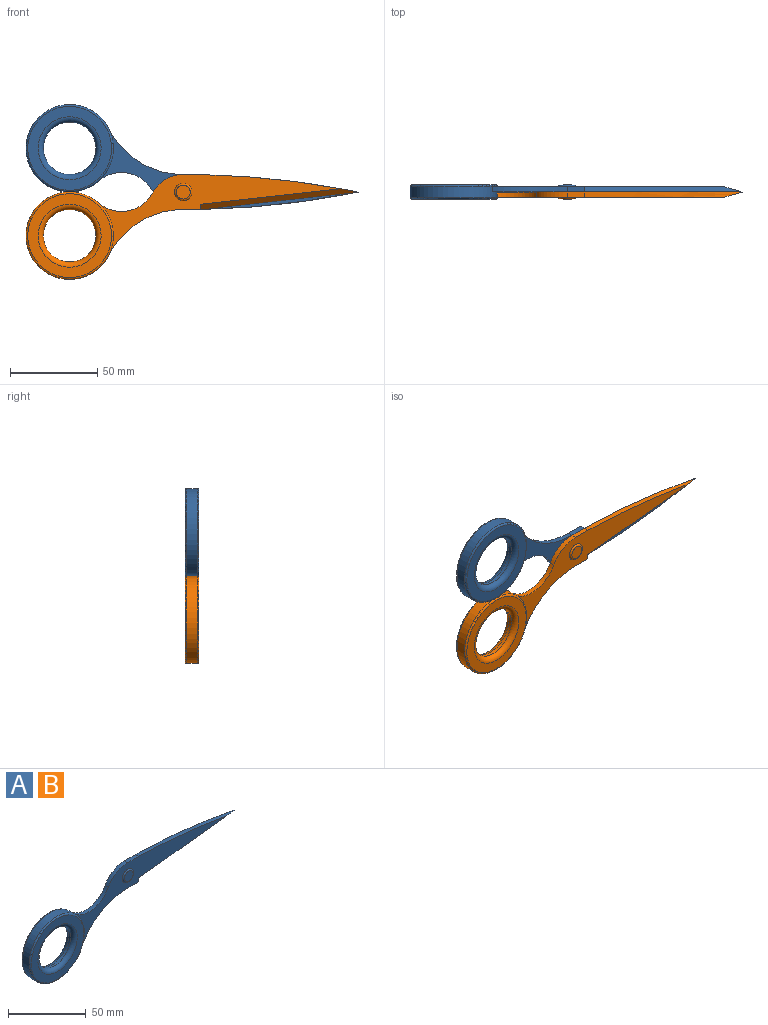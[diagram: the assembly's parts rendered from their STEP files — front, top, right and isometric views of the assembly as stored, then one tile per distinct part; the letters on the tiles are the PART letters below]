
ASSEMBLY  parts=2 mates=1
PART A: 20 faces, bbox 192.1x8x62.1 mm
  f0: plane 138.66x46.27mm, normal (0,-1,0), area 1503.1mm2, adj f2,f3,f4,f5,f6,f8,f13,f14
  f1: plane 148.5x46.27mm, normal (0,1,0), area 1837mm2, adj f2,f3,f4,f5,f6,f7,f8,f13
  f2: plane 10x3mm, normal (0,0,1), area 30mm2, adj f0,f1,f4,f5
  f3: plane 10x3mm, normal (0,0,-1), area 30mm2, adj f0,f1,f8,f14
  f4: cylinder r=500mm len=90mm, axis (0,1,0), area 257.2mm2, adj f0,f1,f2,f13
  f5: cylinder r=20mm len=17.65mm, axis (0,1,0), area 64.9mm2, adj f0,f1,f2,f6
  f6: cylinder r=20mm len=30.85mm, axis (0,1,0), area 108.1mm2, adj f0,f1,f5,f7
  f7: cylinder r=25mm len=50mm, axis (0,1,0), area 843.7mm2, adj f1,f6,f8,f18,f19
  f8: cylinder r=47.81mm len=42.68mm, axis (0,1,0), area 158.3mm2, adj f0,f1,f3,f7
  f9: plane 48x48mm, normal (0,1,0), area 791.7mm2, adj f15,f18
  f10: cylinder r=15mm len=30mm, axis (0,1,0), area 188.5mm2, adj f15,f16
  f11: plane 48x48mm, normal (0,-1,0), area 791.7mm2, adj f16,f19
  f12: plane 8x8mm, normal (0,-1,0), area 50.3mm2, adj f17
  f13: plane 90x11.91mm, normal (0.08,-0.7,-0.7), area 362.3mm2, adj f0,f1,f4,f14
  f14: plane 3x3mm, normal (1,0,0), area 4.5mm2, adj f0,f3,f13
  f15: torus R=18mm, axis (0,-1,0), area 476.4mm2, adj f9,f10
  f16: torus R=18mm, axis (0,-1,0), area 476.4mm2, adj f10,f11
  f17: torus R=4mm, axis (0,-1,0), area 45.8mm2, adj f0,f12
  f18: torus R=24mm, axis (0,-1,0), area 243.2mm2, adj f7,f9
  f19: torus R=24mm, axis (0,-1,0), area 243.2mm2, adj f0,f7,f11
PART B: same geometry as A
PLACE A rot(axis=(1,0,0),180deg) t=(61.99,133.76,160.26)mm
PLACE B t=(61.99,133.76,160.26)mm fixed
MATE revolute B.f17 <-> A.f17  axis (0,-1,0) through (61.99,133.76,160.26)mm
